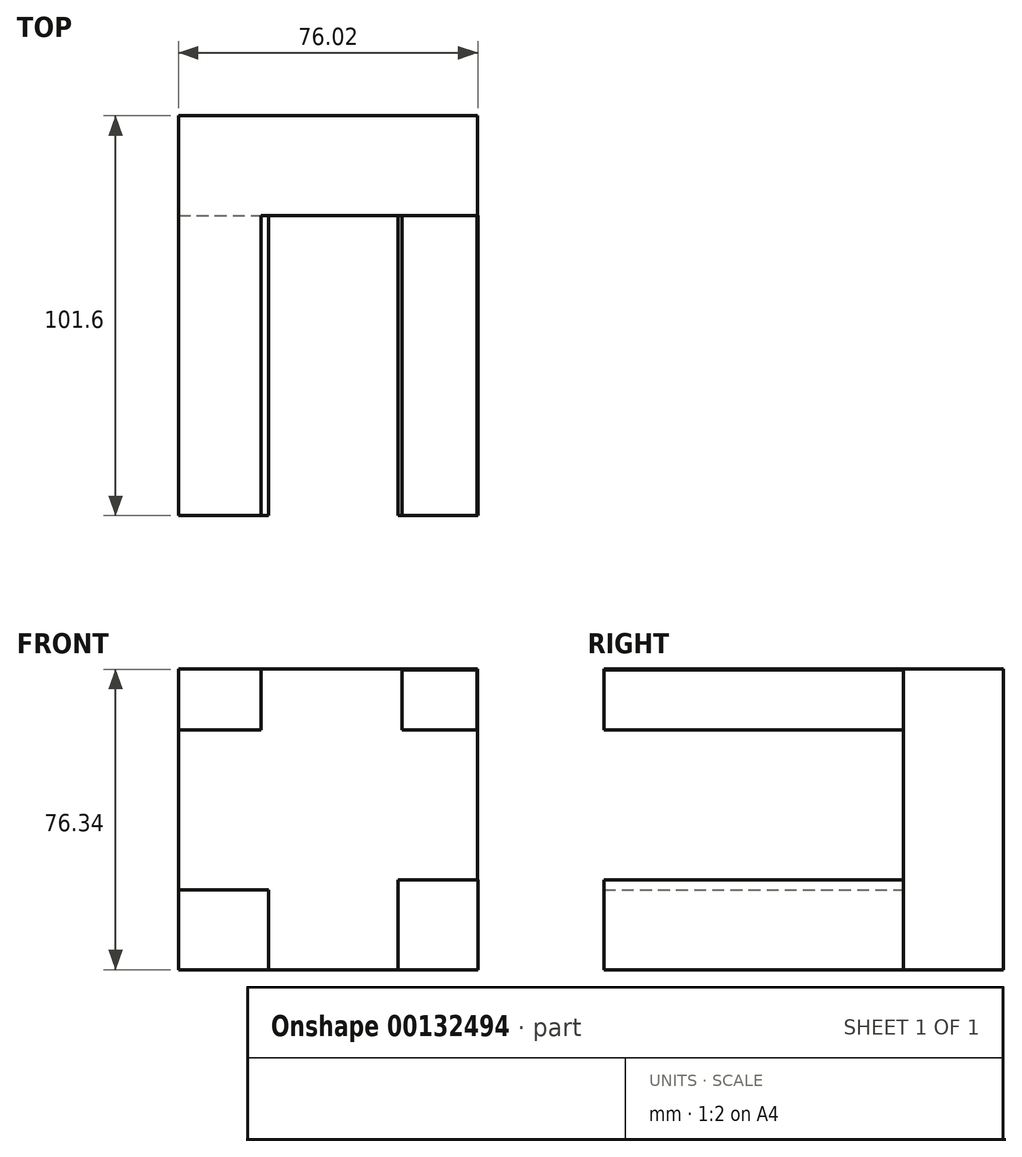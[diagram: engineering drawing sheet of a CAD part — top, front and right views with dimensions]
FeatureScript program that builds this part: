
annotation { "Feature Type Name" : "Feature", "Feature Type Description" : "" }
export const myFeature = defineFeature(function(context is Context, id is Id, definition is map)
    precondition{}
    {
        {
            var Q0;
            Q0=qCreatedBy(makeId("Front.planeOp"),FACE);
            var sketch = newSketch(context, id + "F0", { "sketchPlane" : qUnion([Q0])});
            skLineSegment(sketch, "E0", {"start": v(0, 0) * mm, "end": v(0, 76.58) * mm});
            skLineSegment(sketch, "E1.bottom", {"start": v(1.42, 0) * mm, "end": v(77.37, 0) * mm});
            skLineSegment(sketch, "E1.top", {"start": v(1.42, 76.34) * mm, "end": v(77.37, 76.34) * mm});
            skLineSegment(sketch, "E1.left", {"start": v(1.42, 0) * mm, "end": v(1.42, 76.34) * mm});
            skLineSegment(sketch, "E1.right", {"start": v(77.37, 0) * mm, "end": v(77.37, 76.34) * mm});
            skSolve(sketch);
        }
        {
            var Q0;
            Q0 = qSketchRegion(id + "F0", true);
            extrude(context, id + "F1", {"entities" : qUnion([Q0]), "depth" : 25.4 * mm});
        }
        {
            var Q0;
            Q0=makeQuery(id+"F1.opExtrude","CAP_FACE",FACE,{"disambiguationData":[OSD([sQuery(id+"F0.wireOp",EDGE,"E1.bottom"),sQuery(id+"F0.wireOp",EDGE,"E1.top"),sQuery(id+"F0.wireOp",EDGE,"E1.left"),sQuery(id+"F0.wireOp",EDGE,"E1.right")])],"isStart":false});
            var sketch = newSketch(context, id + "F2", { "sketchPlane" : qUnion([Q0])});
            skLineSegment(sketch, "E2.bottom", {"start": v(1.42, 0) * mm, "end": v(24.28, 0) * mm});
            skLineSegment(sketch, "E2.top", {"start": v(1.42, 20.32) * mm, "end": v(24.28, 20.32) * mm});
            skLineSegment(sketch, "E2.left", {"start": v(1.42, 0) * mm, "end": v(1.42, 20.32) * mm});
            skLineSegment(sketch, "E2.right", {"start": v(24.28, 0) * mm, "end": v(24.28, 20.32) * mm});
            skLineSegment(sketch, "E3.bottom", {"start": v(1.42, 76.34) * mm, "end": v(22.38, 76.34) * mm});
            skLineSegment(sketch, "E3.top", {"start": v(1.42, 60.94) * mm, "end": v(22.38, 60.94) * mm});
            skLineSegment(sketch, "E3.left", {"start": v(1.42, 76.34) * mm, "end": v(1.42, 60.94) * mm});
            skLineSegment(sketch, "E3.right", {"start": v(22.38, 76.34) * mm, "end": v(22.38, 60.94) * mm});
            skSolve(sketch);
        }
        {
            var Q0;
            Q0 = qSketchRegion(id + "F2", true);
            extrude(context, id + "F3", {"entities" : qUnion([Q0]), "operationType" : NewBodyOperationType.ADD, "depth" : 76.2 * mm});
        }
        {
            var Q0;
            Q0=makeQuery(id+"F1.opExtrude","CAP_FACE",FACE,{"disambiguationData":[OSD([sQuery(id+"F0.wireOp",EDGE,"E1.bottom"),sQuery(id+"F0.wireOp",EDGE,"E1.top"),sQuery(id+"F0.wireOp",EDGE,"E1.left"),sQuery(id+"F0.wireOp",EDGE,"E1.right")])],"isStart":false});
            var sketch = newSketch(context, id + "F4", { "sketchPlane" : qUnion([Q0])});
            skSolve(sketch);
        }
        {
            var Q0;
            Q0=makeQuery(id+"F4.imprint","IMPRINT",FACE,{"disambiguationData":[TD([[makeQuery(id+"F4.imprint","IMPRINT",EDGE,{"derivedFrom":makeQuery(id+"F1.opExtrude","CAP_EDGE",EDGE,{"disambiguationData":[OSD([sQuery(id+"F0.wireOp",EDGE,"E1.right")])],"isStart":false})}),1.0]])]});
            var sketch = newSketch(context, id + "F5", { "sketchPlane" : qUnion([Q0])});
            skLineSegment(sketch, "E4.bottom", {"start": v(77.44, 0) * mm, "end": v(57.12, 0) * mm});
            skLineSegment(sketch, "E4.top", {"start": v(77.44, 22.86) * mm, "end": v(57.12, 22.86) * mm});
            skLineSegment(sketch, "E4.left", {"start": v(77.44, 0) * mm, "end": v(77.44, 22.86) * mm});
            skLineSegment(sketch, "E4.right", {"start": v(57.12, 0) * mm, "end": v(57.12, 22.86) * mm});
            skLineSegment(sketch, "E5.bottom", {"start": v(77.23, 76.11) * mm, "end": v(58.22, 76.11) * mm});
            skLineSegment(sketch, "E5.top", {"start": v(77.23, 60.94) * mm, "end": v(58.22, 60.94) * mm});
            skLineSegment(sketch, "E5.left", {"start": v(77.23, 76.11) * mm, "end": v(77.23, 60.94) * mm});
            skLineSegment(sketch, "E5.right", {"start": v(58.22, 76.11) * mm, "end": v(58.22, 60.94) * mm});
            skSolve(sketch);
        }
        {
            var Q0;
            Q0 = qSketchRegion(id + "F5", true);
            extrude(context, id + "F6", {"entities" : qUnion([Q0]), "operationType" : NewBodyOperationType.ADD, "depth" : 76.2 * mm});
        }
    });
